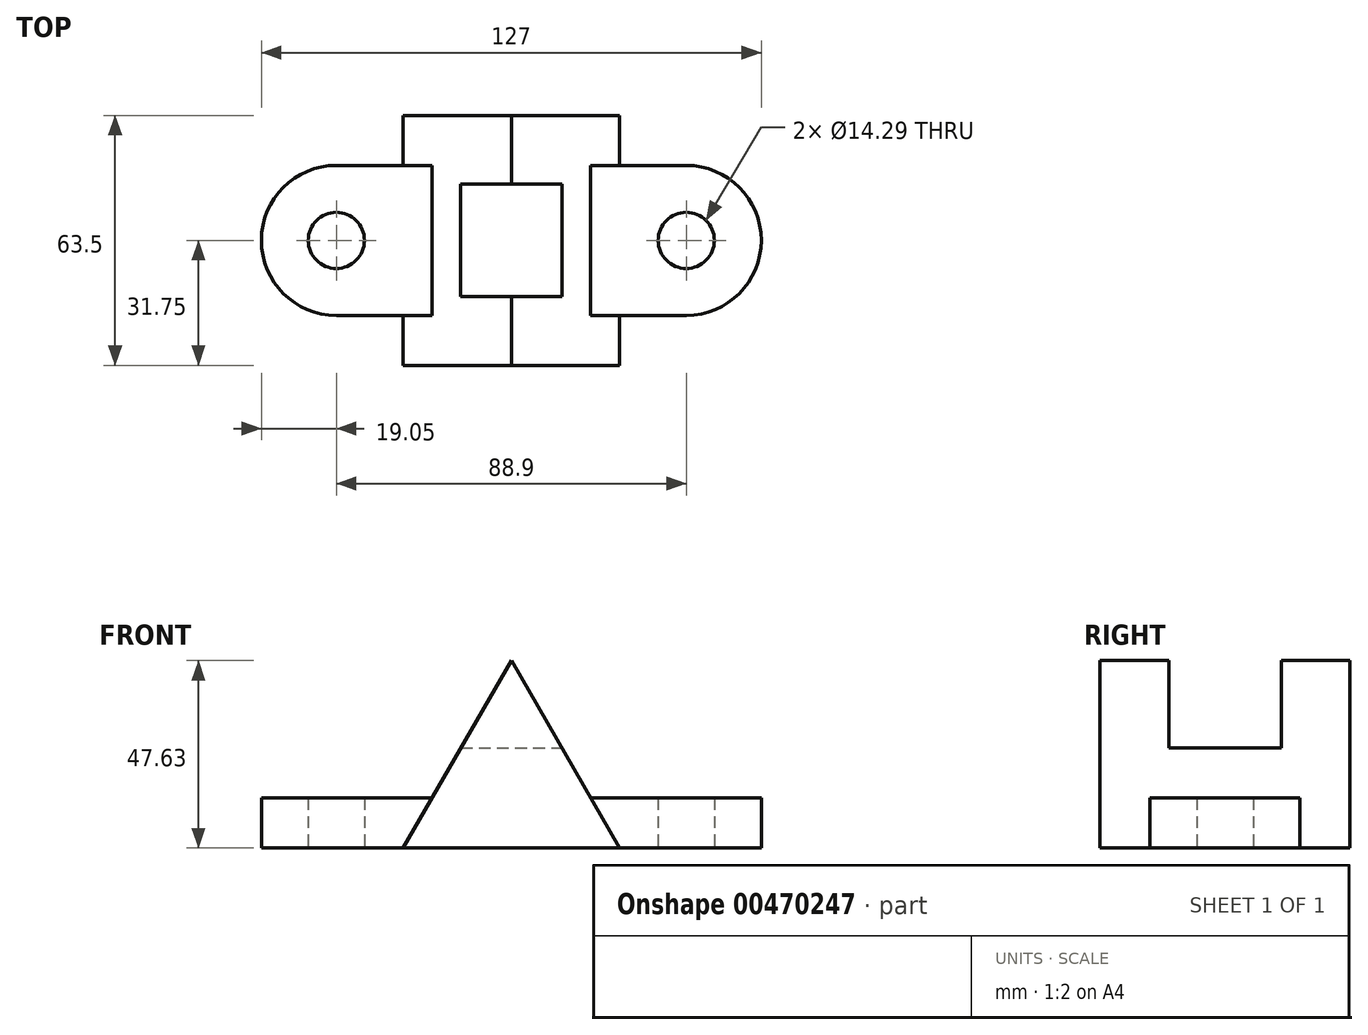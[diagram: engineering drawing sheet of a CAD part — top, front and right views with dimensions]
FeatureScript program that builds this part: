
annotation { "Feature Type Name" : "Feature", "Feature Type Description" : "" }
export const myFeature = defineFeature(function(context is Context, id is Id, definition is map)
    precondition{}
    {
        {
            var Q0;
            Q0=qCreatedBy(makeId("Top.planeOp"),FACE);
            var sketch = newSketch(context, id + "F0", { "sketchPlane" : qUnion([Q0])});
            skLineSegment(sketch, "E0", {"start": v(0, 0) * mm, "end": v(44.45, 0) * mm});
            skLineSegment(sketch, "E1", {"start": v(0, 0) * mm, "end": v(-44.45, 0) * mm});
            skCircle(sketch, "E2", {"center": v(-44.45, 0) * mm, "radius": 19.05 * mm});
            skCircle(sketch, "E3", {"center": v(44.45, 0) * mm, "radius": 19.05 * mm});
            skCircle(sketch, "E4", {"center": v(-44.45, 0) * mm, "radius": 7.14 * mm});
            skCircle(sketch, "E5", {"center": v(44.45, 0) * mm, "radius": 7.14 * mm});
            skLineSegment(sketch, "E6", {"start": v(-44.45, 19.05) * mm, "end": v(44.45, 19.05) * mm});
            skLineSegment(sketch, "E7", {"start": v(-44.45, -19.05) * mm, "end": v(44.45, -19.05) * mm});
            skSolve(sketch);
        }
        {
            var Q0;
            Q0 = qSketchRegion(id + "F0", true);
            extrude(context, id + "F1", {"entities" : qUnion([Q0]), "depth" : 12.7 * mm});
        }
        {
            var Q0;
            Q0=qCreatedBy(makeId("Front.planeOp"),FACE);
            var sketch = newSketch(context, id + "F2", { "sketchPlane" : qUnion([Q0])});
            skLineSegment(sketch, "E8", {"start": v(0, 0) * mm, "end": v(0, 47.63) * mm, "construction": true});
            skLineSegment(sketch, "E9", {"start": v(0, 47.62) * mm, "end": v(-27.5, 0) * mm});
            skLineSegment(sketch, "E10", {"start": v(-27.5, 0) * mm, "end": v(27.5, 0) * mm});
            skLineSegment(sketch, "E11", {"start": v(27.5, 0) * mm, "end": v(0, 47.62) * mm});
            skSolve(sketch);
        }
        {
            var Q0;
            Q0 = qSketchRegion(id + "F2", true);
            extrude(context, id + "F3", {"entities" : qUnion([Q0]), "operationType" : NewBodyOperationType.ADD, "depth" : 63.5 * mm, "symmetric" : true});
        }
        {
            var Q0;
            Q0=qCreatedBy(makeId("Right.planeOp"),FACE);
            var sketch = newSketch(context, id + "F4", { "sketchPlane" : qUnion([Q0])});
            skPoint(sketch, "E12", {"position": v(0, 47.62) * mm});
            skLineSegment(sketch, "E13", {"start": v(0, 47.62) * mm, "end": v(-14.29, 47.62) * mm});
            skLineSegment(sketch, "E14", {"start": v(0, 47.62) * mm, "end": v(14.29, 47.62) * mm});
            skLineSegment(sketch, "E15", {"start": v(-14.29, 47.62) * mm, "end": v(-14.29, 25.4) * mm});
            skLineSegment(sketch, "E16", {"start": v(-14.29, 25.4) * mm, "end": v(14.29, 25.4) * mm});
            skLineSegment(sketch, "E17", {"start": v(14.29, 25.4) * mm, "end": v(14.29, 47.62) * mm});
            skSolve(sketch);
        }
        {
            var Q0;
            Q0 = qSketchRegion(id + "F4", true);
            extrude(context, id + "F5", {"entities" : qUnion([Q0]), "operationType" : NewBodyOperationType.REMOVE, "oppositeDirection" : true, "depth" : 50.8 * mm, "symmetric" : true});
        }
    });
